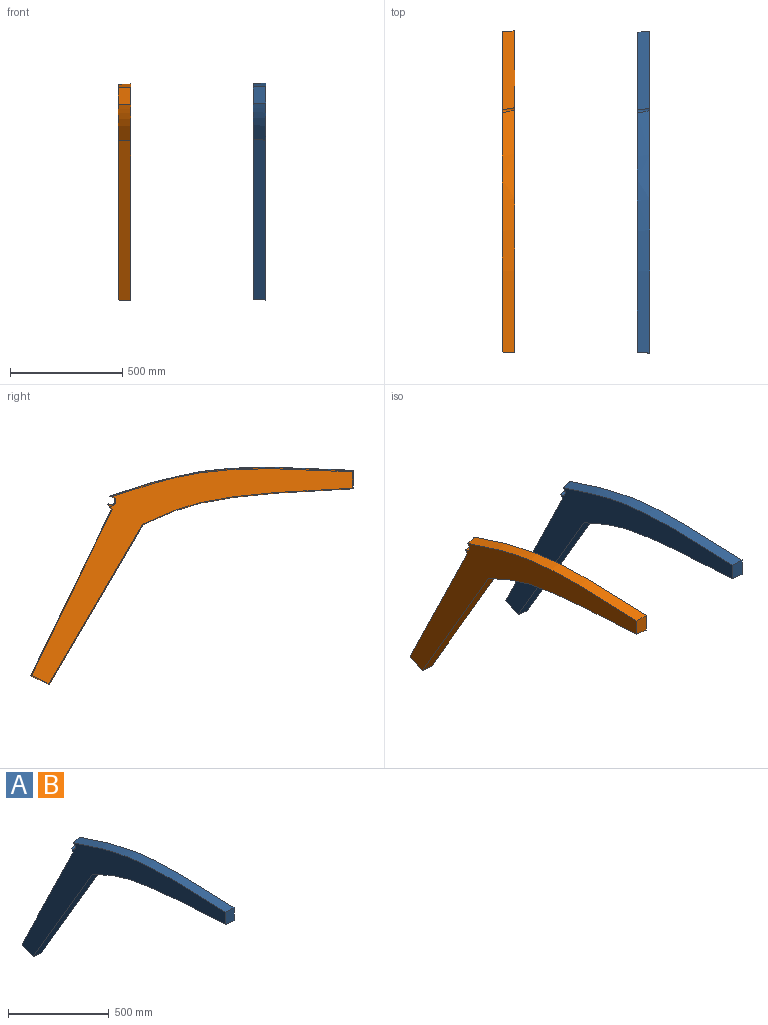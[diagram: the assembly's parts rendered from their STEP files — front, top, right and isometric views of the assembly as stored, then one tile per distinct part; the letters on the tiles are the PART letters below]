
ASSEMBLY  parts=2 mates=1
PART A: 10 faces, bbox 68.6x1443.4x966.2 mm
  f0: plane 738.97x362.09mm, normal (-0.05,0.9,0.44), area 46959.9mm2, adj f1,f7,f8,f9
  f1: plane 57.15x23.18mm, normal (-0.05,0.84,-0.54), area 1317.7mm2, adj f0,f2,f8,f9
  f2: cone r=22.83mm half-angle=3deg, axis (-1,0,0), area 4011.1mm2, adj f1,f3,f8,f9
  f3: bspline ~1097.14x132.92mm, area 62282.9mm2, adj f2,f4,f8,f9
  f4: plane 78.89x57.15mm, normal (-0.05,-1,0), area 4351.7mm2, adj f3,f5,f8,f9
  f5: bspline ~946.2x164.82mm, area 54719.7mm2, adj f4,f6,f8,f9
  f6: plane 714.09x417.6mm, normal (-0.05,-0.86,-0.5), area 47140.1mm2, adj f5,f7,f8,f9
  f7: plane 82.9x57.15mm, normal (-0.05,0.44,-0.9), area 5108.5mm2, adj f0,f6,f8,f9
  f8: plane 1433.87x965.22mm, normal (1,0,0), area 232581.5mm2, adj f0,f1,f2,f3,f4,f5,f6,f7
  f9: plane 1426.87x958.31mm, normal (-1,0,0), area 220757.9mm2, adj f0,f1,f2,f3,f4,f5,f6,f7
PART B: same geometry as A
PLACE A rot(axis=(0,-1,0),0deg) t=(68.56,-1005.08,415.54)mm
PLACE B t=(-532.2,-1002.96,411.88)mm
MATE parallel A.f9 <-> B.f8  axis (-1,0,0) through (68.56,-71.4,181.36)mm
